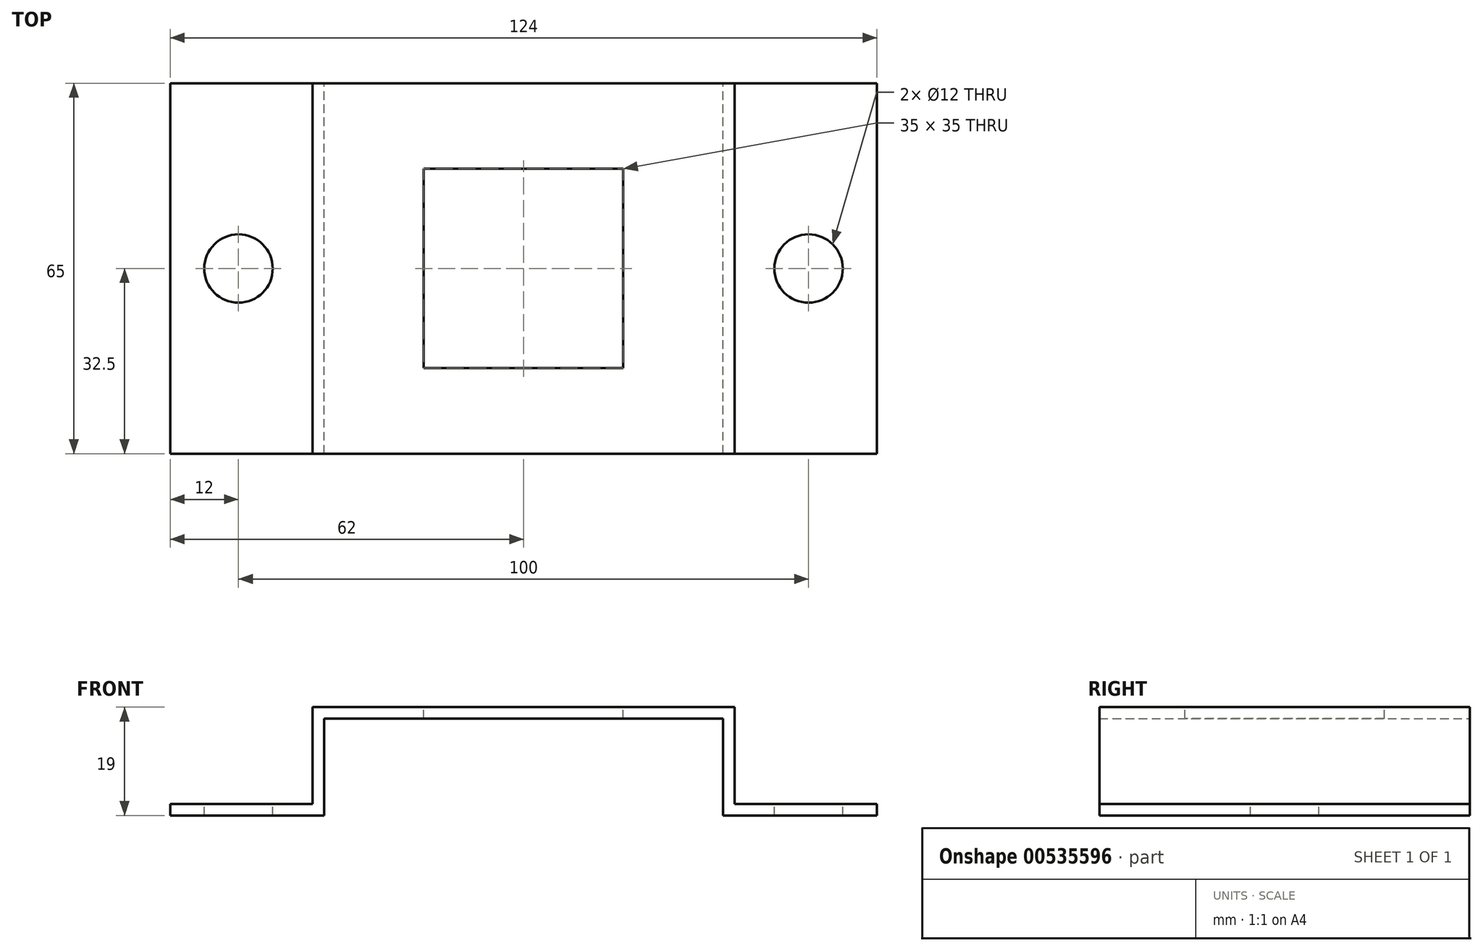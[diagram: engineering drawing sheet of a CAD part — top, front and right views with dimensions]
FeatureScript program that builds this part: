
annotation { "Feature Type Name" : "Feature", "Feature Type Description" : "" }
export const myFeature = defineFeature(function(context is Context, id is Id, definition is map)
    precondition{}
    {
        {
            var Q0;
            Q0=qCreatedBy(makeId("Top.planeOp"),FACE);
            var sketch = newSketch(context, id + "F0", { "sketchPlane" : qUnion([Q0])});
            skPoint(sketch, "E0", {"position": v(0, 0) * mm});
            skLineSegment(sketch, "E1.bottom", {"start": v(0, 17.5) * mm, "end": v(17.5, 17.5) * mm});
            skLineSegment(sketch, "E1.top", {"start": v(0, -17.5) * mm, "end": v(17.5, -17.5) * mm});
            skLineSegment(sketch, "E1.right", {"start": v(17.5, 17.5) * mm, "end": v(17.5, -17.5) * mm});
            skLineSegment(sketch, "E2", {"start": v(0, 32.5) * mm, "end": v(35, 32.5) * mm});
            skPoint(sketch, "E3", {"position": v(0, 32.5) * mm});
            skLineSegment(sketch, "E4", {"start": v(35, 32.5) * mm, "end": v(35, 0) * mm});
            skLineSegment(sketch, "E5.MirrorCS", {"start": v(35, -32.5) * mm, "end": v(35, 0) * mm});
            skLineSegment(sketch, "E6.MirrorCS", {"start": v(0, -32.5) * mm, "end": v(35, -32.5) * mm});
            skLineSegment(sketch, "E7", {"start": v(0, 32.5) * mm, "end": v(0, 17.5) * mm});
            skLineSegment(sketch, "E8.trimOffspring", {"start": v(0, -17.5) * mm, "end": v(0, -32.5) * mm});
            skLineSegment(sketch, "E9", {"start": v(35, 32.5) * mm, "end": v(37, 32.5) * mm});
            skLineSegment(sketch, "E10", {"start": v(37, 32.5) * mm, "end": v(37, -32.5) * mm});
            skLineSegment(sketch, "E11", {"start": v(0, 32.5) * mm, "end": v(0, -32.5) * mm, "construction": true});
            skLineSegment(sketch, "E12", {"start": v(35, -32.5) * mm, "end": v(37, -32.5) * mm});
            skSolve(sketch);
        }
        {
            var Q0;
            Q0=makeQuery(id+"F0.imprint","IMPRINT",FACE,{"disambiguationData":[TD([[makeQuery(id+"F0.imprint","IMPRINT",EDGE,{"derivedFrom":sQuery(id+"F0.wireOp",EDGE,"E1.bottom")}),1.0]])]});
            extrude(context, id + "F1", {"entities" : qUnion([Q0]), "oppositeDirection" : true, "depth" : 2 * mm, "offsetDistance" : 25 * mm});
        }
        {
            var Q0;
            Q0=makeQuery(id+"F0.imprint","IMPRINT",FACE,{"disambiguationData":[TD([[makeQuery(id+"F0.imprint","IMPRINT",EDGE,{"derivedFrom":sQuery(id+"F0.wireOp",EDGE,"E4")}),1.0]])]});
            extrude(context, id + "F2", {"entities" : qUnion([Q0]), "operationType" : NewBodyOperationType.ADD, "oppositeDirection" : true, "depth" : 19 * mm, "offsetDistance" : 25 * mm});
        }
        {
            var Q0;
            Q0=makeQuery(id+"F2.opExtrude","SWEPT_FACE",FACE,{"disambiguationData":[OSD([sQuery(id+"F0.wireOp",EDGE,"E10")])]});
            var sketch = newSketch(context, id + "F3", { "sketchPlane" : qUnion([Q0])});
            skLineSegment(sketch, "E13", {"start": v(-32.5, -17) * mm, "end": v(32.5, -17) * mm});
            skSolve(sketch);
        }
        {
            var Q0;
            Q0 = qSketchRegion(id + "F3", true);
            var Q1;
            {var subQ0=sQuery(id+"F3.wireOp",EDGE,"E13");Q1=makeQuery(id+"F3.imprint","IMPRINT",FACE,{"disambiguationData":[TD([[makeQuery(id+"F3.imprint","IMPRINT",EDGE,{"derivedFrom":subQ0}),-1.0]])]});}
            extrude(context, id + "F4", {"entities" : qUnion([Q0, Q1]), "operationType" : NewBodyOperationType.ADD, "depth" : 25 * mm, "offsetDistance" : 25 * mm});
        }
        {
            var Q0;
            Q0=makeQuery(id+"F4.opExtrude","SWEPT_FACE",FACE,{"disambiguationData":[OSD([sQuery(id+"F3.wireOp",EDGE,"E13")])]});
            var sketch = newSketch(context, id + "F5", { "sketchPlane" : qUnion([Q0])});
            skCircle(sketch, "E14", {"center": v(50, 0) * mm, "radius": 6 * mm});
            skSolve(sketch);
        }
        {
            var Q0;
            Q0=makeQuery(id+"F5.imprint","IMPRINT",FACE,{"disambiguationData":[TD([[makeQuery(id+"F5.imprint","IMPRINT",EDGE,{"derivedFrom":sQuery(id+"F5.wireOp",EDGE,"E14")}),1.0]])]});
            extrude(context, id + "F6", {"entities" : qUnion([Q0]), "operationType" : NewBodyOperationType.REMOVE, "endBound" : BoundingType.THROUGH_ALL, "oppositeDirection" : true, "depth" : 25 * mm, "offsetDistance" : 25 * mm});
        }
        {
            var Q0;
            Q0=makeQuery(id+"F1.opExtrude","SWEPT_BODY",BODY,{"disambiguationData":[OSD([sQuery(id+"F0.wireOp",EDGE,"E1.bottom"),sQuery(id+"F0.wireOp",EDGE,"E1.top"),sQuery(id+"F0.wireOp",EDGE,"E1.right"),sQuery(id+"F0.wireOp",EDGE,"E2"),sQuery(id+"F0.wireOp",EDGE,"E4"),sQuery(id+"F0.wireOp",EDGE,"E5.MirrorCS"),sQuery(id+"F0.wireOp",EDGE,"E6.MirrorCS"),sQuery(id+"F0.wireOp",EDGE,"E7"),sQuery(id+"F0.wireOp",EDGE,"E8.trimOffspring")])]});
            var Q1;
            Q1=makeQuery(id+"F1.opExtrude","SWEPT_FACE",FACE,{"disambiguationData":[OSD([sQuery(id+"F0.wireOp",EDGE,"E7")])]});
            mirror(context, id + "F7", {"operationType" : NewBodyOperationType.ADD, "entities" : qUnion([Q0]), "mirrorPlane" : qUnion([Q1])});
        }
    });
